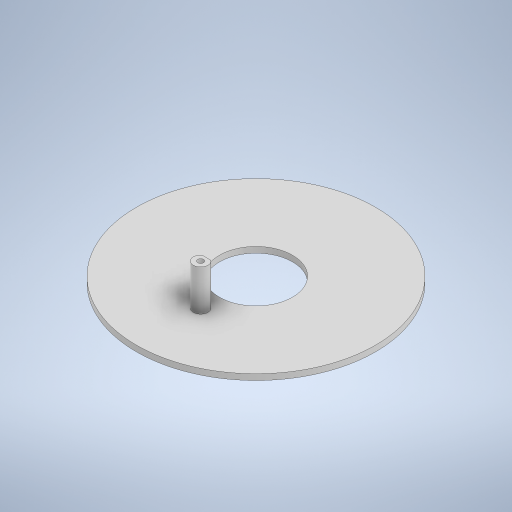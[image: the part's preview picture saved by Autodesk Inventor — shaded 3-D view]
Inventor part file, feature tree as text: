
AUTODESK INVENTOR PART (.ipt)
format: ipt  version: 2024 (Build 280153000, 153)  size: 249,344 bytes
history: native  units: in
note: dims shown in document units (in); Inventor stores cm internally (conversion verified against a paired STEP export)
features: extrude x4, sketch x4
ambient origin geometry x8: Origin, YZ Plane, XZ Plane, XY Plane, X Axis, Y Axis, Z Axis, Center Point
bodies: Solid1 (feature_tree)
feature tree (8):
  extrude  "Extrusion1"  Depth=0.9843in
  extrude  "Extrusion2"  Depth=0.0787in
  extrude  "Extrusion3"  Depth=0.1969in
  extrude  "Extrusion4"  Depth=0.0787in
  sketch  "Sketch1"  dims[d0=3.2283in d1=0.9843in]
  sketch  "Sketch2"  dims[d2=0.0787in d3=0.0in d4=0.748in]
  sketch  "Sketch3"  dims[d5=90.0deg d6=0.1969in]
  sketch  "Sketch4"  dims[d7=0.5512in d8=0.0in d9=0.0787in d10=0.5512in d11=0.0in d12=0.0197in d13=0.1181in d14=0.0197in d15=0.1181in d16=0.5512in d17=0.0in d18=0.0197in d19=0.0344in]
